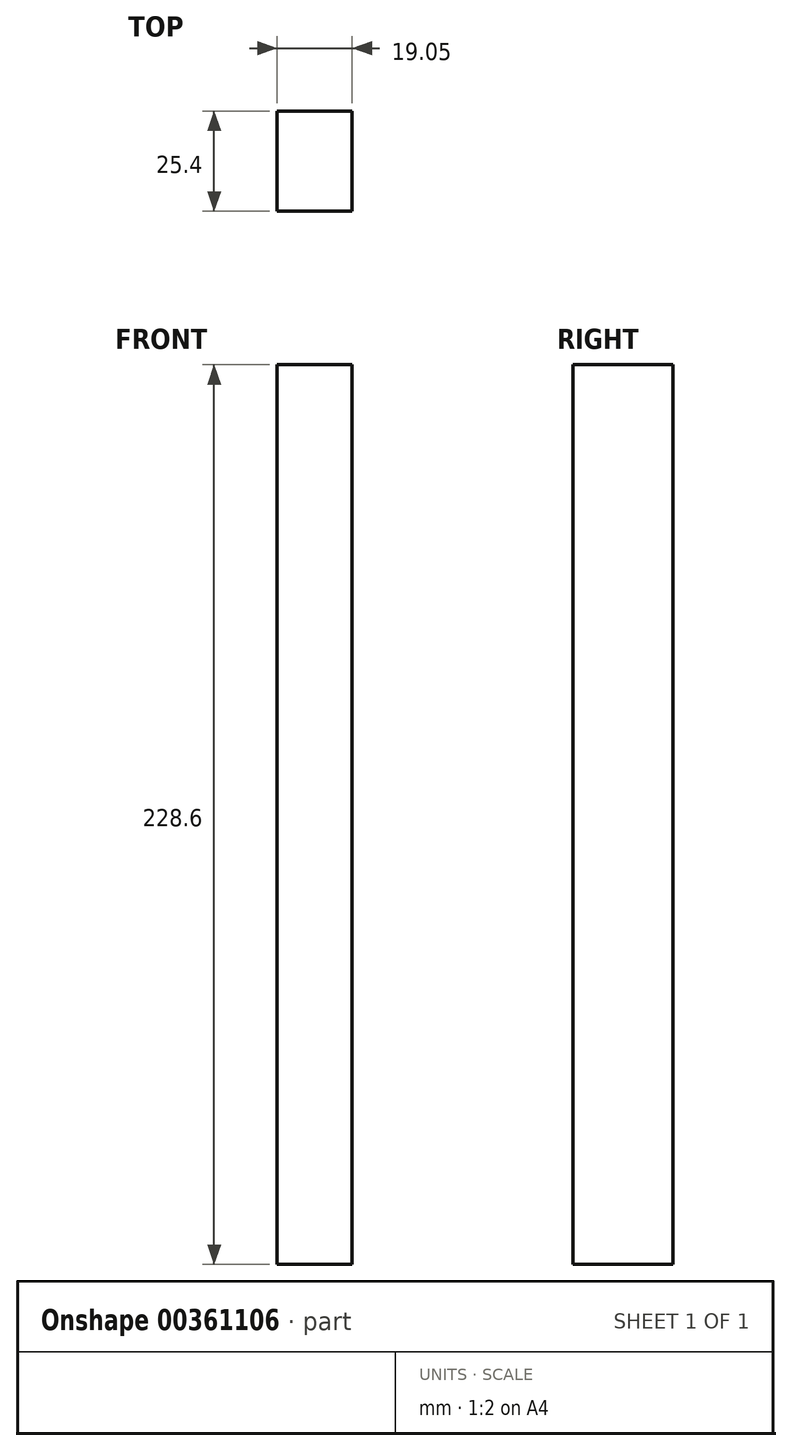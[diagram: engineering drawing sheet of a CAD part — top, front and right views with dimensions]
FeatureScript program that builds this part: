
annotation { "Feature Type Name" : "Feature", "Feature Type Description" : "" }
export const myFeature = defineFeature(function(context is Context, id is Id, definition is map)
    precondition{}
    {
        {
            var Q0;
            Q0=qCreatedBy(makeId("Right.planeOp"),FACE);
            var sketch = newSketch(context, id + "F0", { "sketchPlane" : qUnion([Q0])});
            skLineSegment(sketch, "E0.bottom", {"start": v(-115.08, 83.28) * mm, "end": v(-89.68, 83.28) * mm});
            skLineSegment(sketch, "E0.top", {"start": v(-115.08, -145.32) * mm, "end": v(-89.68, -145.32) * mm});
            skLineSegment(sketch, "E0.left", {"start": v(-115.08, 83.28) * mm, "end": v(-115.08, -145.32) * mm});
            skLineSegment(sketch, "E0.right", {"start": v(-89.68, 83.28) * mm, "end": v(-89.68, -145.32) * mm});
            skSolve(sketch);
        }
        {
            var Q0;
            Q0=qSketchRegion(id+"F0",true);
            extrude(context, id + "F1", {"entities" : qUnion([Q0]), "depth" : 19.05 * mm});
        }
    });
